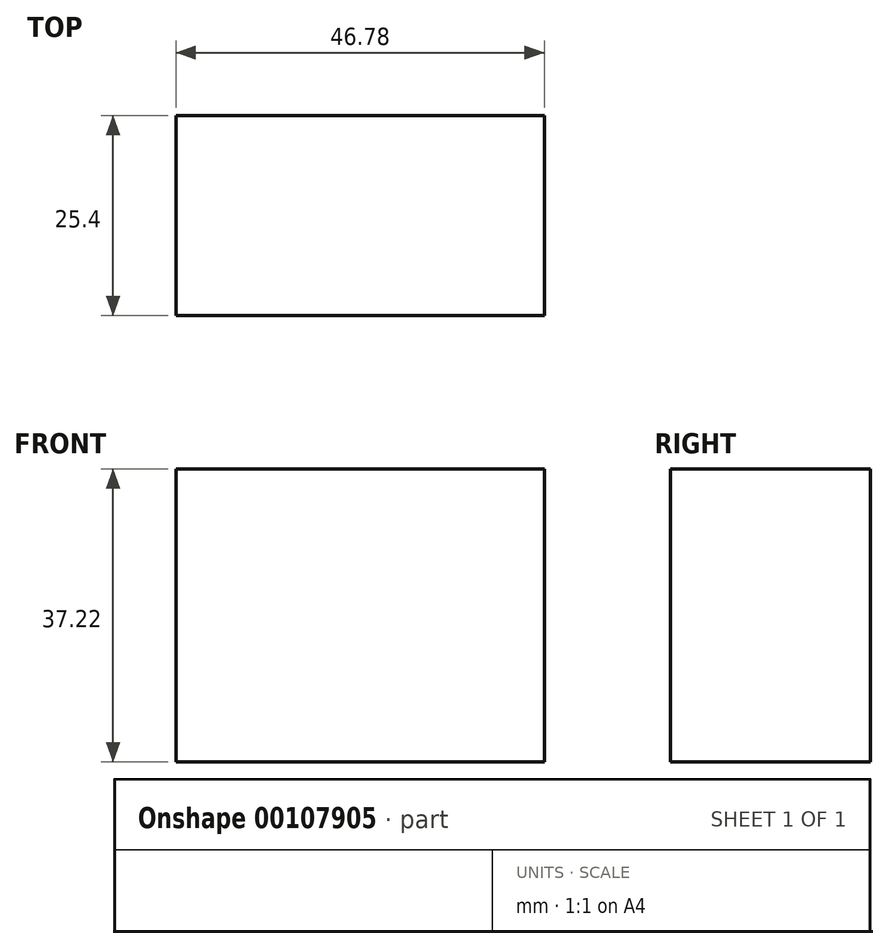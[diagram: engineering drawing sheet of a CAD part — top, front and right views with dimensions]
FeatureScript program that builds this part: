
annotation { "Feature Type Name" : "Feature", "Feature Type Description" : "" }
export const myFeature = defineFeature(function(context is Context, id is Id, definition is map)
    precondition{}
    {
        {
            var Q0;
            Q0=qCreatedBy(makeId("Front.planeOp"),FACE);
            var sketch = newSketch(context, id + "F0", { "sketchPlane" : qUnion([Q0])});
            skLineSegment(sketch, "E0.bottom", {"start": v(0, 0) * mm, "end": v(46.78, 0) * mm});
            skLineSegment(sketch, "E0.top", {"start": v(0, 37.22) * mm, "end": v(46.78, 37.22) * mm});
            skLineSegment(sketch, "E0.left", {"start": v(0, 0) * mm, "end": v(0, 37.22) * mm});
            skLineSegment(sketch, "E0.right", {"start": v(46.78, 0) * mm, "end": v(46.78, 37.22) * mm});
            skSolve(sketch);
        }
        {
            var Q0;
            Q0 = qSketchRegion(id + "F0", true);
            extrude(context, id + "F1", {"entities" : qUnion([Q0]), "endBound" : BoundingType.SYMMETRIC, "depth" : 25.4 * mm});
        }
    });
